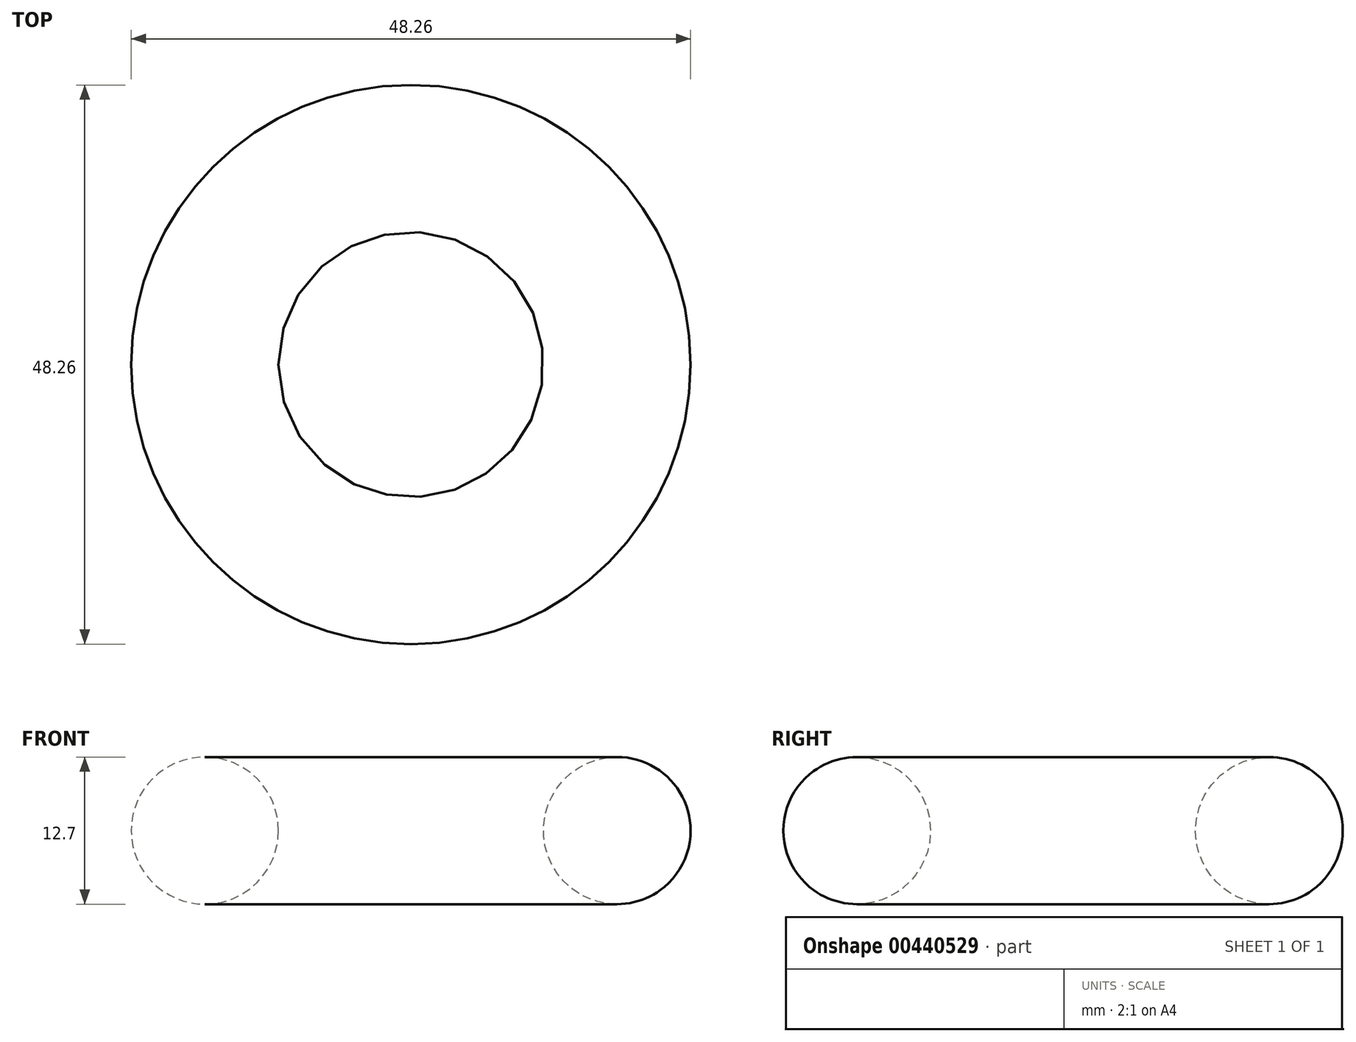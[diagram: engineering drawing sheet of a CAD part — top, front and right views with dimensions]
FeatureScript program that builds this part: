
annotation { "Feature Type Name" : "Feature", "Feature Type Description" : "" }
export const myFeature = defineFeature(function(context is Context, id is Id, definition is map)
    precondition{}
    {
        {
            var Q0;
            Q0=qCreatedBy(makeId("Front.planeOp"),FACE);
            var sketch = newSketch(context, id + "F0", { "sketchPlane" : qUnion([Q0])});
            skCircle(sketch, "E0", {"center": v(17.78, 0) * mm, "radius": 6.35 * mm});
            skLineSegment(sketch, "E1", {"start": v(0, 0) * mm, "end": v(0, 14.62) * mm, "construction": true});
            skSolve(sketch);
        }
        {
            var Q0;
            Q0 = qSketchRegion(id + "F0", true);
            var Q1;
            Q1=sQuery(id+"F0.wireOp",EDGE,"E1");
            revolve(context, id + "F1", {"entities" : qUnion([Q0]), "axis" : qUnion([Q1]), "revolveType" : RevolveType.FULL});
        }
    });
